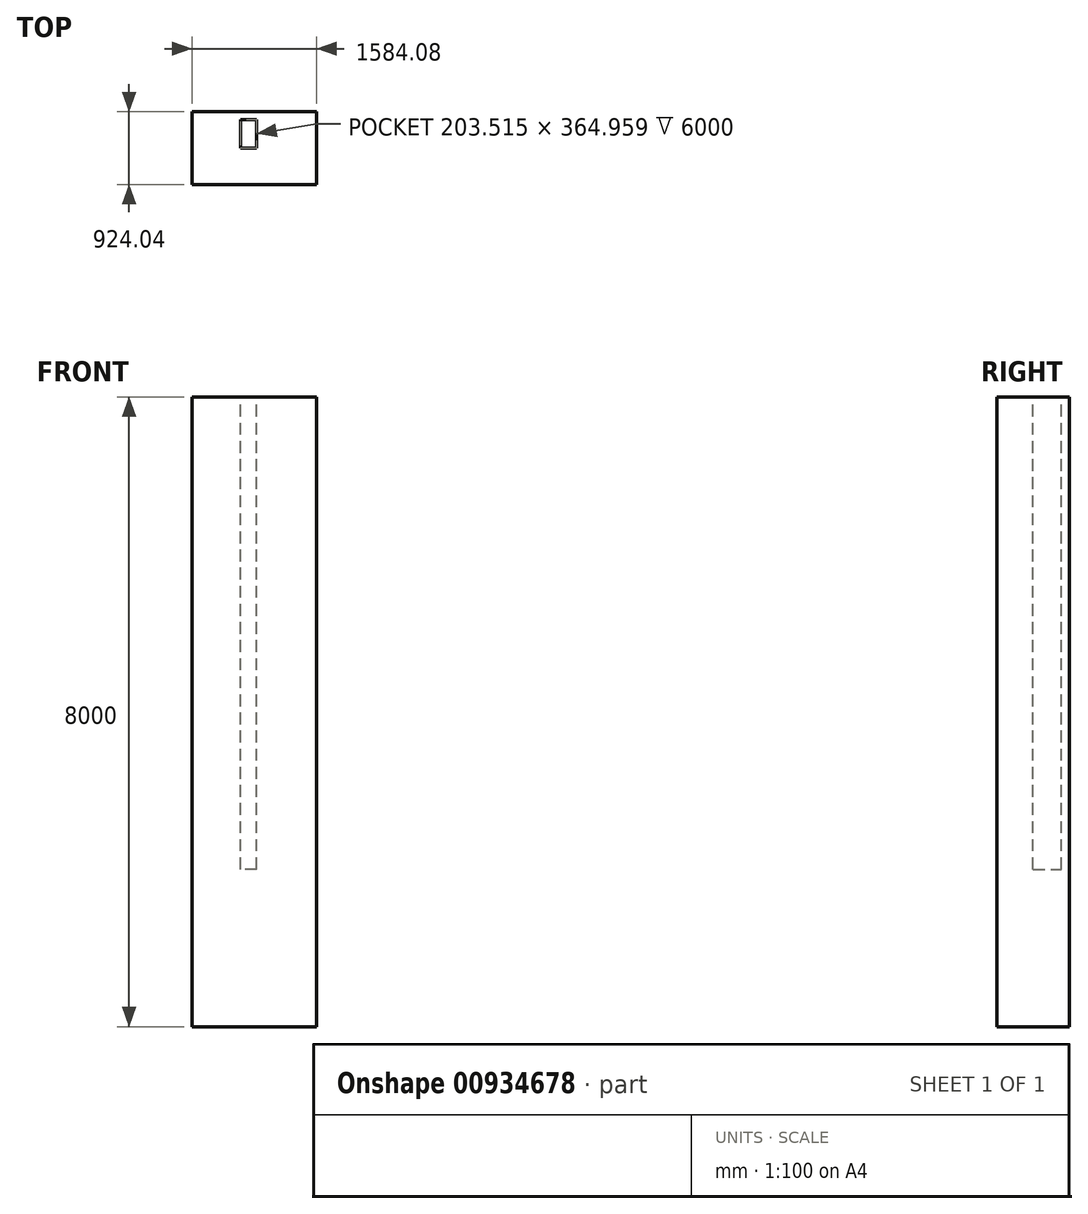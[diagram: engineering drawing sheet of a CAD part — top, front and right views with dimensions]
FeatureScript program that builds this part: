
annotation { "Feature Type Name" : "Feature", "Feature Type Description" : "" }
export const myFeature = defineFeature(function(context is Context, id is Id, definition is map)
    precondition{}
    {
        {
            var Q0;
            Q0=qCreatedBy(makeId("Top.planeOp"),FACE);
            var sketch = newSketch(context, id + "F0", { "sketchPlane" : qUnion([Q0])});
            skLineSegment(sketch, "E0.bottom", {"start": v(526.93, -257.98) * mm, "end": v(-529.24, -257.98) * mm});
            skLineSegment(sketch, "E0.top", {"start": v(526.93, 301.85) * mm, "end": v(-529.24, 301.85) * mm});
            skLineSegment(sketch, "E0.left", {"start": v(526.93, -257.98) * mm, "end": v(526.93, 301.85) * mm});
            skLineSegment(sketch, "E0.right", {"start": v(-529.24, -257.98) * mm, "end": v(-529.24, 301.85) * mm});
            skSolve(sketch);
        }
        {
            var Q0;
            Q0=makeQuery(id+"F0.imprint","IMPRINT",FACE,{"disambiguationData":[TD([[makeQuery(id+"F0.imprint","IMPRINT",EDGE,{"derivedFrom":sQuery(id+"F0.wireOp",EDGE,"E0.bottom")}),-1.0]])]});
            var sketch = newSketch(context, id + "F1", { "sketchPlane" : qUnion([Q0])});
            skLineSegment(sketch, "E1.bottom", {"start": v(761.3, -383.53) * mm, "end": v(-822.78, -383.53) * mm});
            skLineSegment(sketch, "E1.top", {"start": v(761.3, 540.5) * mm, "end": v(-822.78, 540.5) * mm});
            skLineSegment(sketch, "E1.left", {"start": v(761.3, -383.53) * mm, "end": v(761.3, 540.5) * mm});
            skLineSegment(sketch, "E1.right", {"start": v(-822.78, -383.53) * mm, "end": v(-822.78, 540.5) * mm});
            skSolve(sketch);
        }
        {
            var Q0;
            Q0 = qSketchRegion(id + "F1", true);
            extrude(context, id + "F2", {"entities" : qUnion([Q0]), "depth" : 8000 * mm, "offsetDistance" : 25 * mm});
        }
        {
            var Q0;
            Q0=makeQuery(id+"F2.opExtrude","CAP_FACE",FACE,{"disambiguationData":[OSD([sQuery(id+"F1.wireOp",EDGE,"E1.bottom"),sQuery(id+"F1.wireOp",EDGE,"E1.top"),sQuery(id+"F1.wireOp",EDGE,"E1.left"),sQuery(id+"F1.wireOp",EDGE,"E1.right")])],"isStart":false});
            var sketch = newSketch(context, id + "F3", { "sketchPlane" : qUnion([Q0])});
            skLineSegment(sketch, "E2.bottom", {"start": v(0, 76.55) * mm, "end": v(-203.52, 76.55) * mm});
            skLineSegment(sketch, "E2.top", {"start": v(0, 441.5) * mm, "end": v(-203.52, 441.5) * mm});
            skLineSegment(sketch, "E2.left", {"start": v(0, 76.55) * mm, "end": v(0, 441.5) * mm});
            skLineSegment(sketch, "E2.right", {"start": v(-203.52, 76.55) * mm, "end": v(-203.52, 441.5) * mm});
            skSolve(sketch);
        }
        {
            var Q0;
            Q0=makeQuery(id+"F3.imprint","IMPRINT",FACE,{"disambiguationData":[TD([[makeQuery(id+"F3.imprint","IMPRINT",EDGE,{"derivedFrom":sQuery(id+"F3.wireOp",EDGE,"E2.bottom")}),-1.0]])]});
            extrude(context, id + "F4", {"entities" : qUnion([Q0]), "operationType" : NewBodyOperationType.REMOVE, "oppositeDirection" : true, "depth" : 6000 * mm, "offsetDistance" : 25 * mm});
        }
    });
